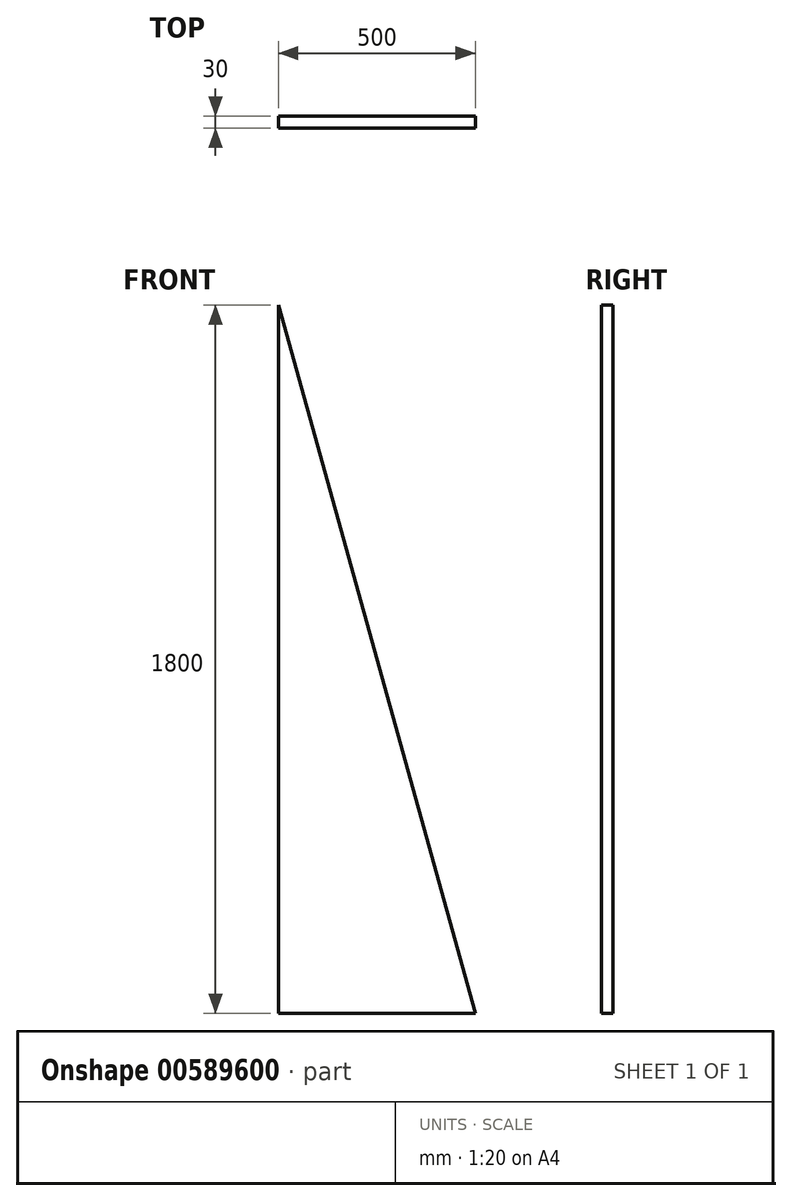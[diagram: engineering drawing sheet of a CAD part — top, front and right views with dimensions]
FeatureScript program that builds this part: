
annotation { "Feature Type Name" : "Feature", "Feature Type Description" : "" }
export const myFeature = defineFeature(function(context is Context, id is Id, definition is map)
    precondition{}
    {
        {
            var Q0;
            Q0=qCreatedBy(makeId("Front.planeOp"),FACE);
            var sketch = newSketch(context, id + "F0", { "sketchPlane" : qUnion([Q0])});
            skLineSegment(sketch, "E0.top", {"start": v(-482.12, -908.42) * mm, "end": v(17.88, -908.42) * mm});
            skLineSegment(sketch, "E0.left", {"start": v(-482.12, 891.58) * mm, "end": v(-482.12, -908.42) * mm});
            skLineSegment(sketch, "E1", {"start": v(-482.12, 891.58) * mm, "end": v(17.88, -908.42) * mm});
            skPoint(sketch, "E0.bottom.end.orphan", {"position": v(17.88, 891.58) * mm});
            skSolve(sketch);
        }
        {
            var Q0;
            Q0=makeQuery(id+"F0.imprint","IMPRINT",FACE,{"disambiguationData":[TD([[makeQuery(id+"F0.imprint","IMPRINT",EDGE,{"derivedFrom":sQuery(id+"F0.wireOp",EDGE,"E0.top")}),1.0]])]});
            extrude(context, id + "F1", {"entities" : qUnion([Q0]), "depth" : 30 * mm, "offsetDistance" : 25 * mm});
        }
    });
